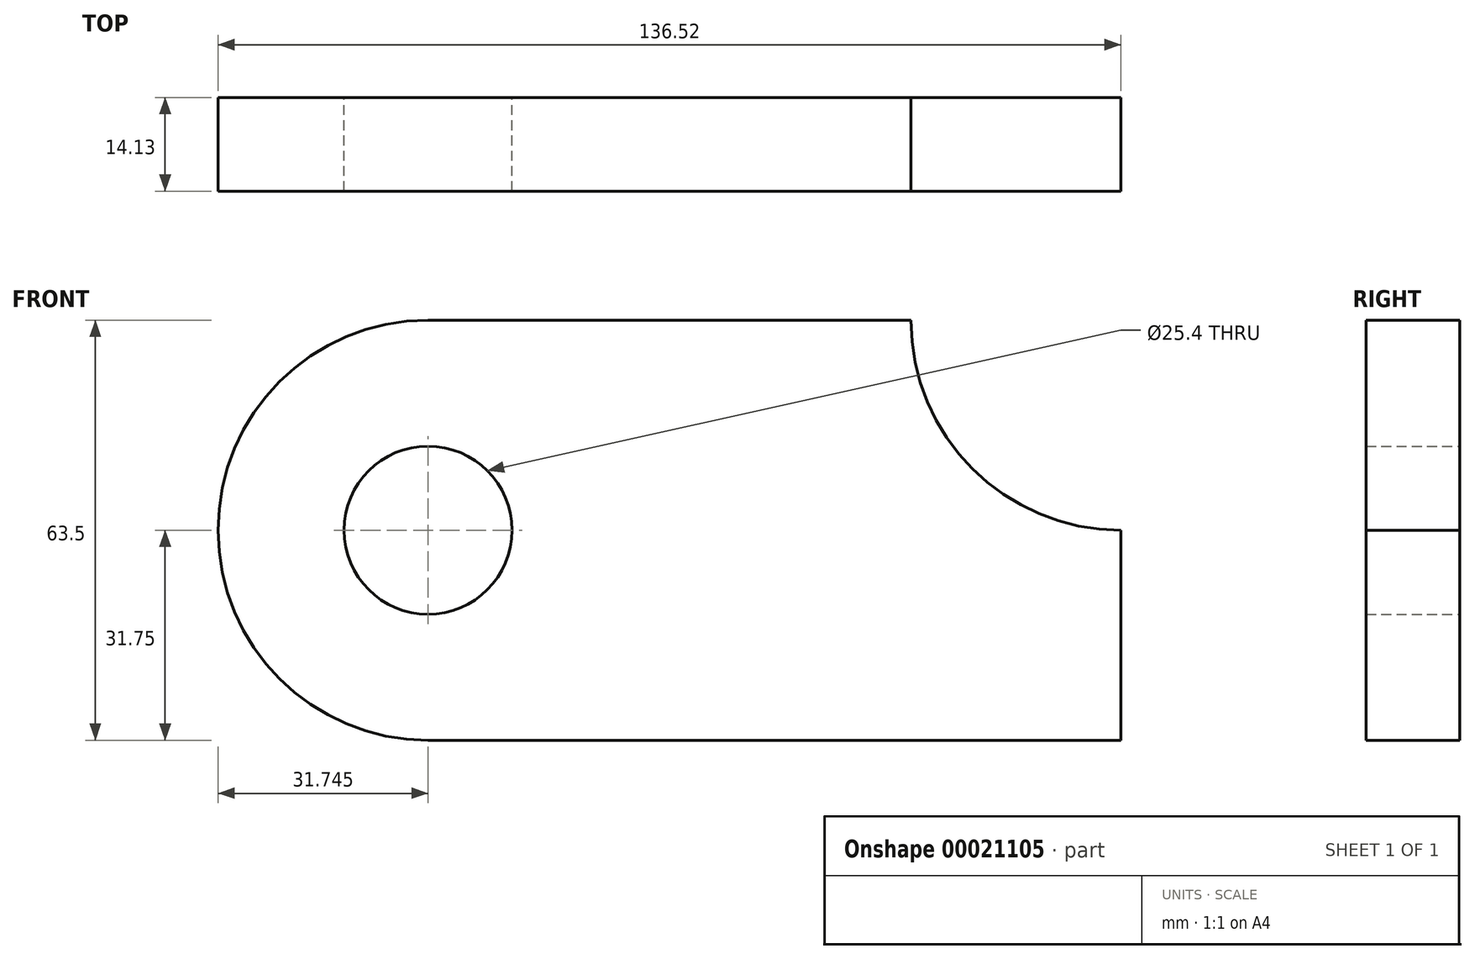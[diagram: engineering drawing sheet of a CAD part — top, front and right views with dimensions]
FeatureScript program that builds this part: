
annotation { "Feature Type Name" : "Feature", "Feature Type Description" : "" }
export const myFeature = defineFeature(function(context is Context, id is Id, definition is map)
    precondition{}
    {
        {
            var Q0;
            Q0=qCreatedBy(makeId("Front.planeOp"),FACE);
            var sketch = newSketch(context, id + "F0", { "sketchPlane" : qUnion([Q0])});
            skLineSegment(sketch, "E0.bottom", {"start": v(0, 0) * mm, "end": v(-104.78, 0) * mm});
            skLineSegment(sketch, "E0.top", {"start": v(0, 63.5) * mm, "end": v(-104.78, 63.5) * mm});
            skLineSegment(sketch, "E0.left", {"start": v(0, 0) * mm, "end": v(0, 63.5) * mm});
            skLineSegment(sketch, "E0.right", {"start": v(-104.78, 0) * mm, "end": v(-104.78, 63.5) * mm});
            skCircle(sketch, "E1", {"center": v(-104.77, 31.75) * mm, "radius": 31.75 * mm});
            skCircle(sketch, "E2", {"center": v(-104.77, 31.75) * mm, "radius": 12.7 * mm});
            skCircle(sketch, "E3", {"center": v(0, 63.5) * mm, "radius": 31.75 * mm});
            skSolve(sketch);
        }
        {
            var Q0;
            {var subQ4=sQuery(id+"F0.wireOp",EDGE,"E0.bottom");Q0=makeQuery(id+"F0.imprint","IMPRINT",FACE,{"disambiguationData":[TD([[makeQuery(id+"F0.imprint","IMPRINT",EDGE,{"derivedFrom":subQ4}),-1.0]])]});}
            var Q1;
            {var subQ0=sQuery(id+"F0.wireOp",EDGE,"E2");var subQ1=sQuery(id+"F0.wireOp",EDGE,"E0.right");var subQ3=makeQuery(id+"F0.imprint","INTERSECT",VERTEX,{"disambiguationData":[OD(0.0)],"derivedFrom":[subQ1,subQ0]});Q1=makeQuery(id+"F0.imprint","IMPRINT",FACE,{"disambiguationData":[TD([[makeQuery(id+"F0.imprint","IMPRINT",EDGE,{"disambiguationData":[TD([[subQ3,1.0]])],"derivedFrom":subQ0}),-1.0]])]});}
            var Q2;
            {var subQ0=sQuery(id+"F0.wireOp",EDGE,"E2");var subQ1=sQuery(id+"F0.wireOp",EDGE,"E0.right");var subQ3=makeQuery(id+"F0.imprint","INTERSECT",VERTEX,{"disambiguationData":[OD(0.0)],"derivedFrom":[subQ1,subQ0]});Q2=makeQuery(id+"F0.imprint","IMPRINT",FACE,{"disambiguationData":[TD([[makeQuery(id+"F0.imprint","IMPRINT",EDGE,{"disambiguationData":[TD([[subQ3,-1.0]])],"derivedFrom":subQ0}),-1.0]])]});}
            extrude(context, id + "F1", {"entities" : qUnion([Q0, Q1, Q2]), "depth" : 14.13 * mm});
        }
    });
